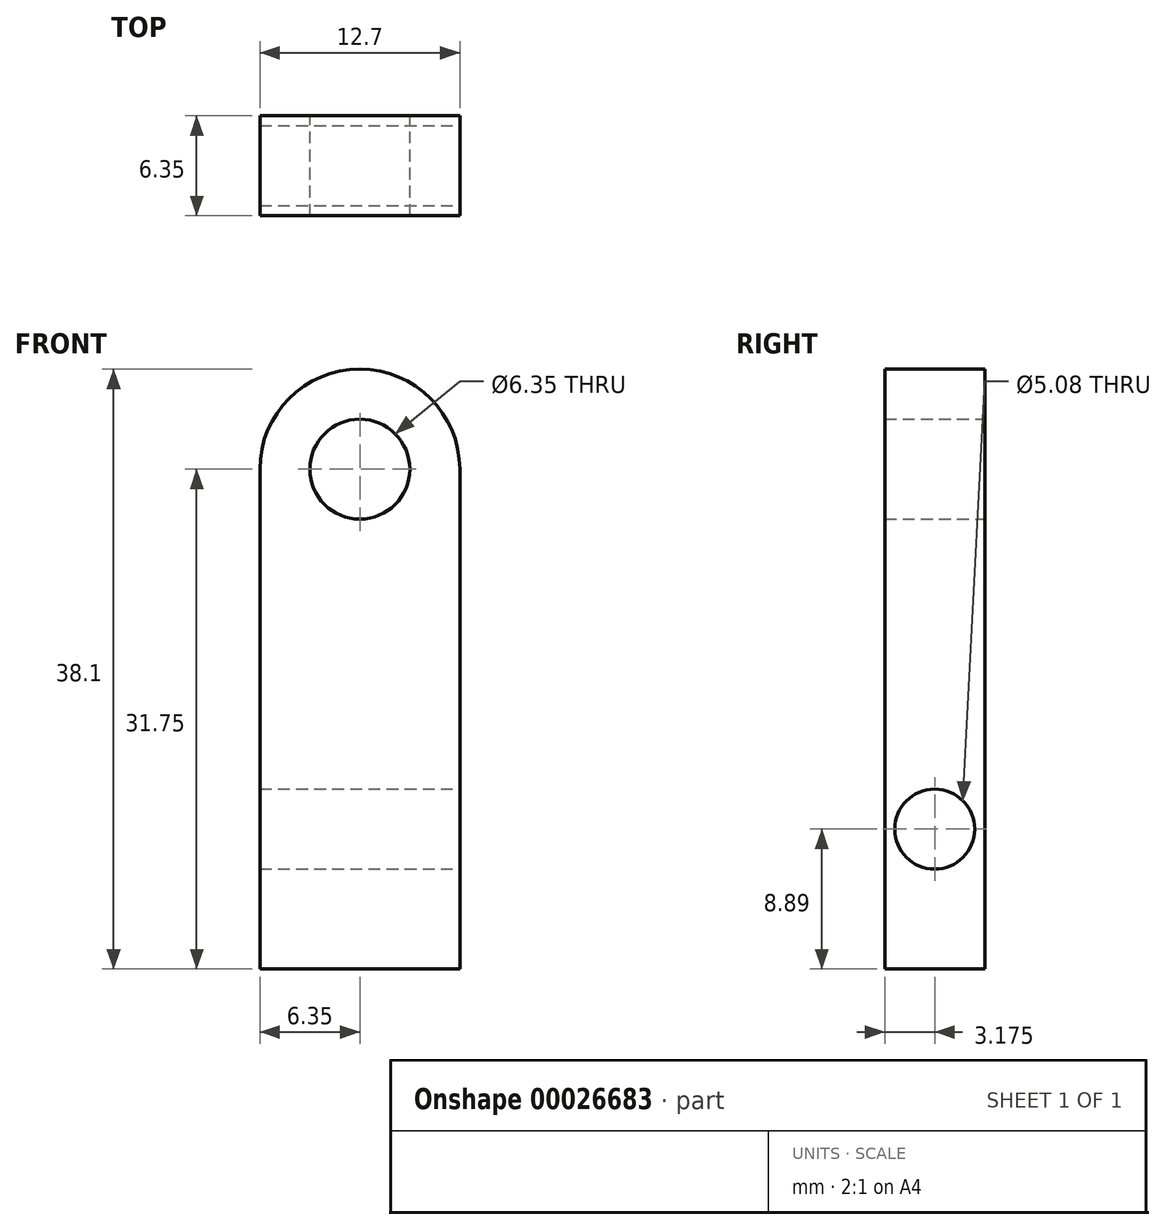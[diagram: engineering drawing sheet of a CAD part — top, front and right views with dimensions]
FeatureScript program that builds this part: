
annotation { "Feature Type Name" : "Feature", "Feature Type Description" : "" }
export const myFeature = defineFeature(function(context is Context, id is Id, definition is map)
    precondition{}
    {
        {
            var Q0;
            Q0=qCreatedBy(makeId("Front.planeOp"),FACE);
            var sketch = newSketch(context, id + "F0", { "sketchPlane" : qUnion([Q0])});
            skLineSegment(sketch, "E0.rect.bottom", {"start": v(-6.35, 31.75) * mm, "end": v(6.35, 31.75) * mm});
            skLineSegment(sketch, "E0.rect.top", {"start": v(-6.35, -31.75) * mm, "end": v(6.35, -31.75) * mm});
            skLineSegment(sketch, "E0.rect.left", {"start": v(-6.35, 31.75) * mm, "end": v(-6.35, -31.75) * mm});
            skLineSegment(sketch, "E0.rect.right", {"start": v(6.35, 31.75) * mm, "end": v(6.35, -31.75) * mm});
            skPoint(sketch, "E0.rect.middle", {"position": v(0, 0) * mm});
            skCircle(sketch, "E1", {"center": v(0, -31.75) * mm, "radius": 6.35 * mm});
            skCircle(sketch, "E2", {"center": v(0, 31.75) * mm, "radius": 6.35 * mm});
            skCircle(sketch, "E3", {"center": v(0, 31.75) * mm, "radius": 3.18 * mm});
            skCircle(sketch, "E4", {"center": v(0, -31.75) * mm, "radius": 3.18 * mm});
            skLineSegment(sketch, "E5", {"start": v(6.35, 0) * mm, "end": v(-6.35, 0) * mm});
            skSolve(sketch);
        }
        {
            var Q0;
            {var subQ0=sQuery(id+"F0.wireOp",EDGE,"E5");Q0=makeQuery(id+"F0.imprint","IMPRINT",FACE,{"disambiguationData":[TD([[makeQuery(id+"F0.imprint","IMPRINT",EDGE,{"derivedFrom":subQ0}),-1.0]])]});}
            var Q1;
            {var subQ0=sQuery(id+"F0.wireOp",EDGE,"E3");var subQ1=sQuery(id+"F0.wireOp",EDGE,"E0.rect.bottom");var subQ3=makeQuery(id+"F0.imprint","INTERSECT",VERTEX,{"disambiguationData":[OD(0.0)],"derivedFrom":[subQ1,subQ0]});Q1=makeQuery(id+"F0.imprint","IMPRINT",FACE,{"disambiguationData":[TD([[makeQuery(id+"F0.imprint","IMPRINT",EDGE,{"disambiguationData":[TD([[subQ3,1.0]])],"derivedFrom":subQ0}),-1.0]])]});}
            var Q2;
            {var subQ0=sQuery(id+"F0.wireOp",EDGE,"E3");var subQ1=sQuery(id+"F0.wireOp",EDGE,"E0.rect.bottom");var subQ3=makeQuery(id+"F0.imprint","INTERSECT",VERTEX,{"disambiguationData":[OD(0.0)],"derivedFrom":[subQ1,subQ0]});Q2=makeQuery(id+"F0.imprint","IMPRINT",FACE,{"disambiguationData":[TD([[makeQuery(id+"F0.imprint","IMPRINT",EDGE,{"disambiguationData":[TD([[subQ3,-1.0]])],"derivedFrom":subQ0}),-1.0]])]});}
            extrude(context, id + "F1", {"entities" : qUnion([Q0, Q1, Q2]), "depth" : 6.35 * mm});
        }
        {
            var Q0;
            Q0=makeQuery(id+"F1.opExtrude","SWEPT_FACE",FACE,{"disambiguationData":[OSD([sQuery(id+"F0.wireOp",EDGE,"E0.rect.right")])]});
            var sketch = newSketch(context, id + "F2", { "sketchPlane" : qUnion([Q0])});
            skCircle(sketch, "E6", {"center": v(-3.17, 8.9) * mm, "radius": 2.54 * mm});
            skSolve(sketch);
        }
        {
            var Q0;
            Q0=makeQuery(id+"F2.imprint","IMPRINT",FACE,{"disambiguationData":[TD([[makeQuery(id+"F2.imprint","IMPRINT",EDGE,{"derivedFrom":sQuery(id+"F2.wireOp",EDGE,"E6")}),1.0]])]});
            extrude(context, id + "F3", {"entities" : qUnion([Q0]), "operationType" : NewBodyOperationType.REMOVE, "oppositeDirection" : true, "depth" : 12.7 * mm});
        }
    });
